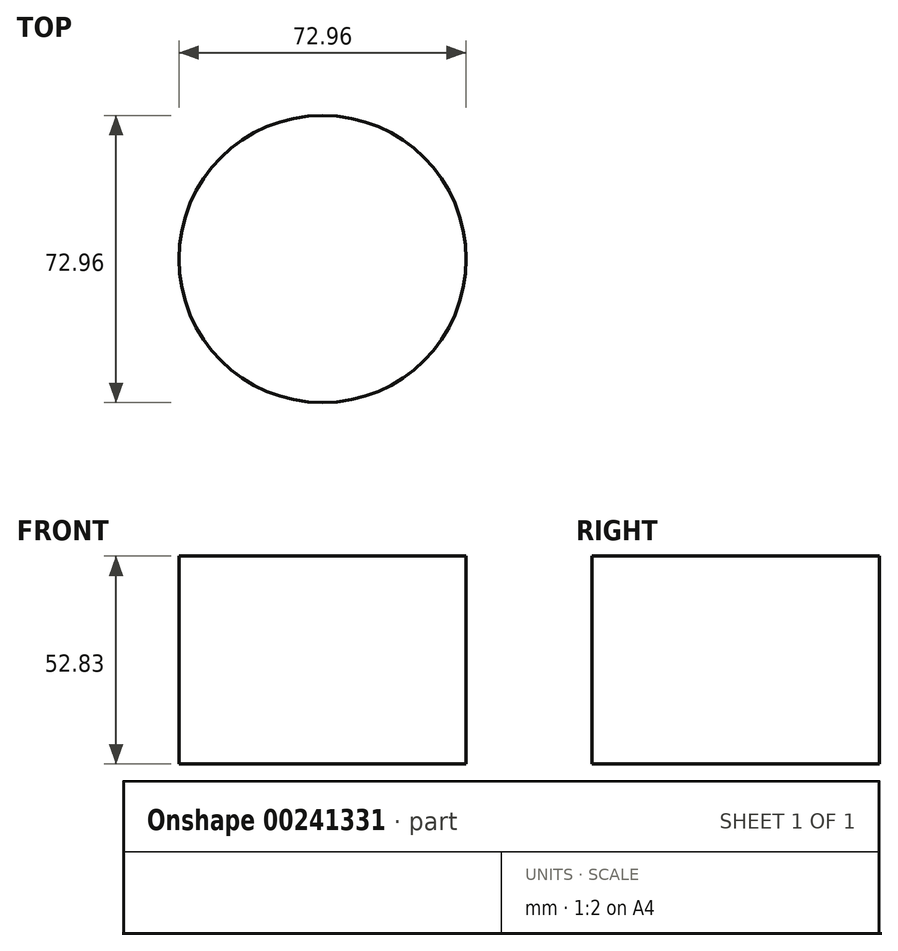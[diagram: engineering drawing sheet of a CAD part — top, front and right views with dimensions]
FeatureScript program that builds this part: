
annotation { "Feature Type Name" : "Feature", "Feature Type Description" : "" }
export const myFeature = defineFeature(function(context is Context, id is Id, definition is map)
    precondition{}
    {
        {
            var Q0;
            Q0=qCreatedBy(makeId("Top.planeOp"),FACE);
            var sketch = newSketch(context, id + "F0", { "sketchPlane" : qUnion([Q0])});
            skCircle(sketch, "E0", {"center": v(0, -3.47) * mm, "radius": 36.48 * mm});
            skSolve(sketch);
        }
        {
            var Q0;
            Q0=makeQuery(id+"F0.imprint","IMPRINT",FACE,{"disambiguationData":[TD([[makeQuery(id+"F0.imprint","IMPRINT",EDGE,{"derivedFrom":sQuery(id+"F0.wireOp",EDGE,"E0")}),1.0]])]});
            extrude(context, id + "F1", {"entities" : qUnion([Q0]), "depth" : 52.83 * mm});
        }
    });
